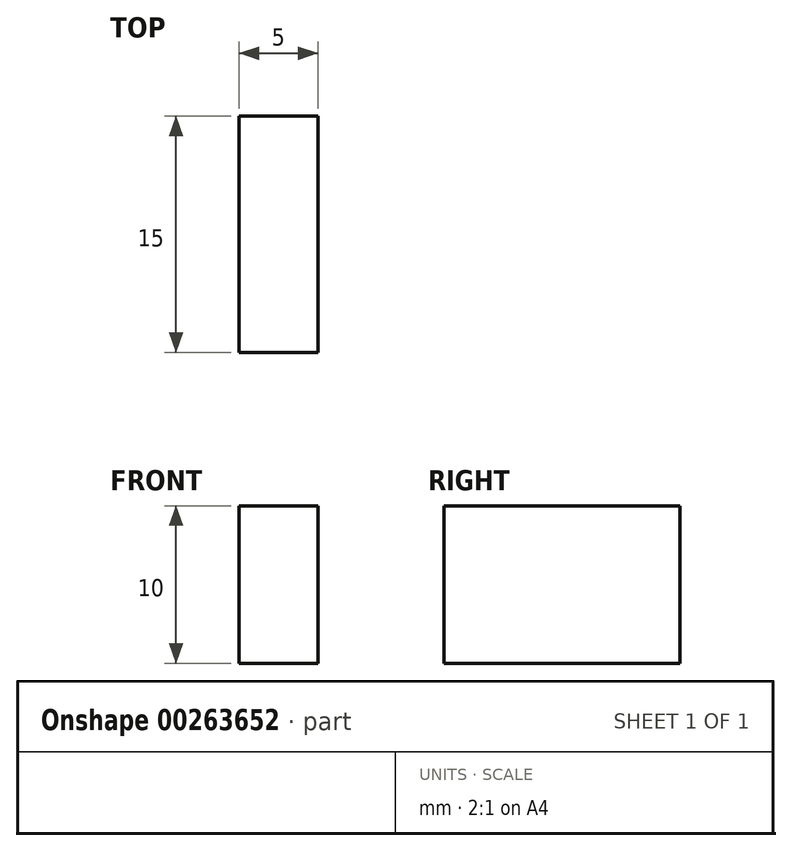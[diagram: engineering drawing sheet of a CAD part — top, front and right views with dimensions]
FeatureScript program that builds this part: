
annotation { "Feature Type Name" : "Feature", "Feature Type Description" : "" }
export const myFeature = defineFeature(function(context is Context, id is Id, definition is map)
    precondition{}
    {
        {
            var Q0;
            Q0=qCreatedBy(makeId("Right.planeOp"),FACE);
            var sketch = newSketch(context, id + "F0", { "sketchPlane" : qUnion([Q0])});
            skLineSegment(sketch, "E0.bottom", {"start": v(0, 0) * mm, "end": v(15, 0) * mm});
            skLineSegment(sketch, "E0.top", {"start": v(0, 10) * mm, "end": v(15, 10) * mm});
            skLineSegment(sketch, "E0.left", {"start": v(0, 0) * mm, "end": v(0, 10) * mm});
            skLineSegment(sketch, "E0.right", {"start": v(15, 0) * mm, "end": v(15, 10) * mm});
            skSolve(sketch);
        }
        {
            var Q0;
            Q0=makeQuery(id+"F0.imprint","IMPRINT",FACE,{"disambiguationData":[TD([[makeQuery(id+"F0.imprint","IMPRINT",EDGE,{"derivedFrom":sQuery(id+"F0.wireOp",EDGE,"E0.bottom")}),1.0]])]});
            extrude(context, id + "F1", {"entities" : qUnion([Q0]), "depth" : 5 * mm});
        }
    });
